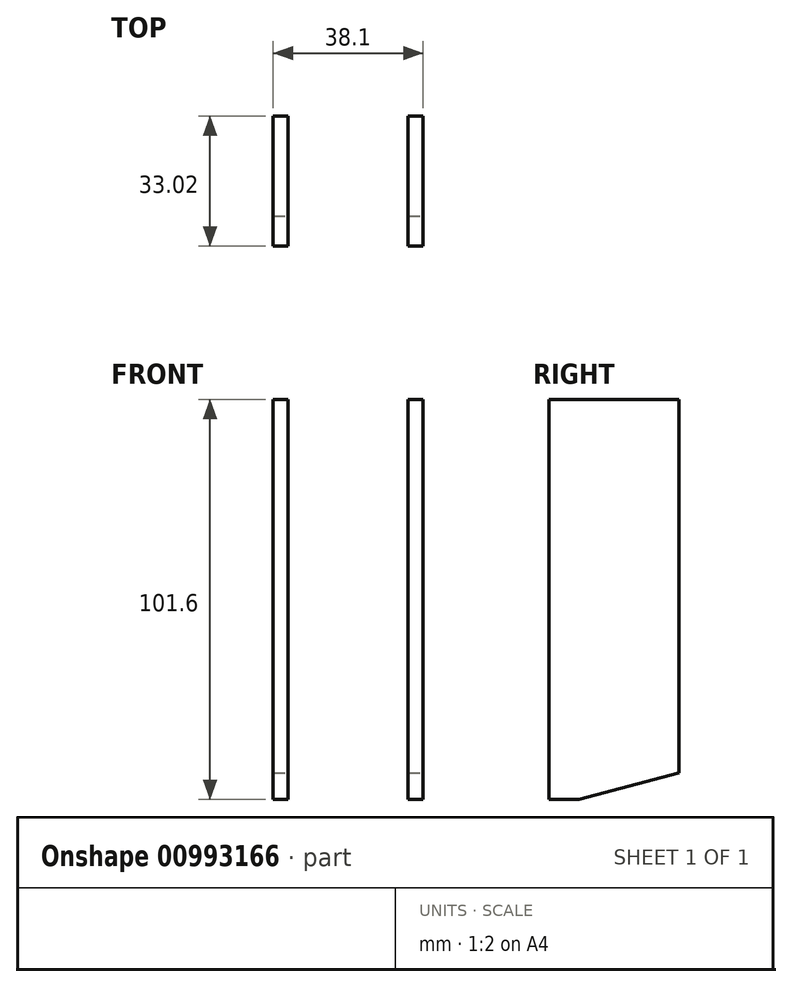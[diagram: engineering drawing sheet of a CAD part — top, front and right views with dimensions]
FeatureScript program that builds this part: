
annotation { "Feature Type Name" : "Feature", "Feature Type Description" : "" }
export const myFeature = defineFeature(function(context is Context, id is Id, definition is map)
    precondition{}
    {
        {
            var Q0;
            Q0=qCreatedBy(makeId("Front.planeOp"),FACE);
            var sketch = newSketch(context, id + "F0", { "sketchPlane" : qUnion([Q0])});
            skLineSegment(sketch, "E0.bottom", {"start": v(-41.17, 82.19) * mm, "end": v(-3.07, 82.19) * mm});
            skLineSegment(sketch, "E0.top", {"start": v(-41.17, -19.41) * mm, "end": v(-3.07, -19.41) * mm});
            skLineSegment(sketch, "E0.left", {"start": v(-41.17, 82.19) * mm, "end": v(-41.17, -19.41) * mm});
            skLineSegment(sketch, "E0.right", {"start": v(-3.07, 82.19) * mm, "end": v(-3.07, -19.41) * mm});
            skLineSegment(sketch, "E1.bottom", {"start": v(-37.36, 82.19) * mm, "end": v(-6.88, 82.19) * mm});
            skLineSegment(sketch, "E1.top", {"start": v(-37.36, -19.41) * mm, "end": v(-6.88, -19.41) * mm});
            skLineSegment(sketch, "E1.left", {"start": v(-37.36, 82.19) * mm, "end": v(-37.36, -19.41) * mm});
            skLineSegment(sketch, "E1.right", {"start": v(-6.88, 82.19) * mm, "end": v(-6.88, -19.41) * mm});
            skSolve(sketch);
        }
        {
            var Q0;
            Q0=makeQuery(id+"F0.imprint","IMPRINT",FACE,{"disambiguationData":[TD([[makeQuery(id+"F0.imprint","IMPRINT",EDGE,{"derivedFrom":sQuery(id+"F0.wireOp",EDGE,"E1.bottom")}),-1.0]])]});
            var Q1;
            {var subQ0=sQuery(id+"F0.wireOp",EDGE,"E0.left");Q1=makeQuery(id+"F0.imprint","IMPRINT",FACE,{"disambiguationData":[TD([[makeQuery(id+"F0.imprint","IMPRINT",EDGE,{"derivedFrom":subQ0}),1.0]])]});}
            var Q2;
            {var subQ0=sQuery(id+"F0.wireOp",EDGE,"E0.right");Q2=makeQuery(id+"F0.imprint","IMPRINT",FACE,{"disambiguationData":[TD([[makeQuery(id+"F0.imprint","IMPRINT",EDGE,{"derivedFrom":subQ0}),-1.0]])]});}
            extrude(context, id + "F1", {"entities" : qUnion([Q0, Q1, Q2]), "depth" : 7.62 * mm, "offsetDistance" : 25.4 * mm});
        }
        {
            var Q0;
            {var subQ0=sQuery(id+"F0.wireOp",EDGE,"E0.right");Q0=makeQuery(id+"F0.imprint","IMPRINT",FACE,{"disambiguationData":[TD([[makeQuery(id+"F0.imprint","IMPRINT",EDGE,{"derivedFrom":subQ0}),-1.0]])]});}
            var Q1;
            {var subQ0=sQuery(id+"F0.wireOp",EDGE,"E0.left");Q1=makeQuery(id+"F0.imprint","IMPRINT",FACE,{"disambiguationData":[TD([[makeQuery(id+"F0.imprint","IMPRINT",EDGE,{"derivedFrom":subQ0}),1.0]])]});}
            extrude(context, id + "F2", {"entities" : qUnion([Q0, Q1]), "operationType" : NewBodyOperationType.ADD, "oppositeDirection" : true, "depth" : 25.4 * mm, "offsetDistance" : 25.4 * mm});
        }
        {
            var Q0;
            {var subQ0=sQuery(id+"F0.wireOp",EDGE,"E0.right");Q0=makeQuery(id+"F2.boolean.opBoolean","MERGE",FACE,{"derivedFrom":[makeQuery(id+"F1.opExtrude","SWEPT_FACE",FACE,{"disambiguationData":[OSD([subQ0])]}),makeQuery(id+"F2.opExtrude","SWEPT_FACE",FACE,{"disambiguationData":[OSD([subQ0])]})]});}
            var sketch = newSketch(context, id + "F3", { "sketchPlane" : qUnion([Q0])});
            skLineSegment(sketch, "E2", {"start": v(25.4, -12.6) * mm, "end": v(0, -19.41) * mm});
            skLineSegment(sketch, "E3", {"start": v(0, -19.41) * mm, "end": v(-7.62, -19.41) * mm});
            skLineSegment(sketch, "E4", {"start": v(-7.62, 82.19) * mm, "end": v(25.4, 82.19) * mm});
            skSolve(sketch);
        }
        {
            var Q0;
            {var subQ0=sQuery(id+"F3.wireOp",EDGE,"E2");Q0=makeQuery(id+"F3.imprint","IMPRINT",FACE,{"disambiguationData":[TD([[makeQuery(id+"F3.imprint","IMPRINT",EDGE,{"derivedFrom":subQ0}),1.0]])]});}
            extrude(context, id + "F4", {"entities" : qUnion([Q0]), "operationType" : NewBodyOperationType.REMOVE, "oppositeDirection" : true, "depth" : 50.8 * mm, "offsetDistance" : 25.4 * mm});
        }
    });
